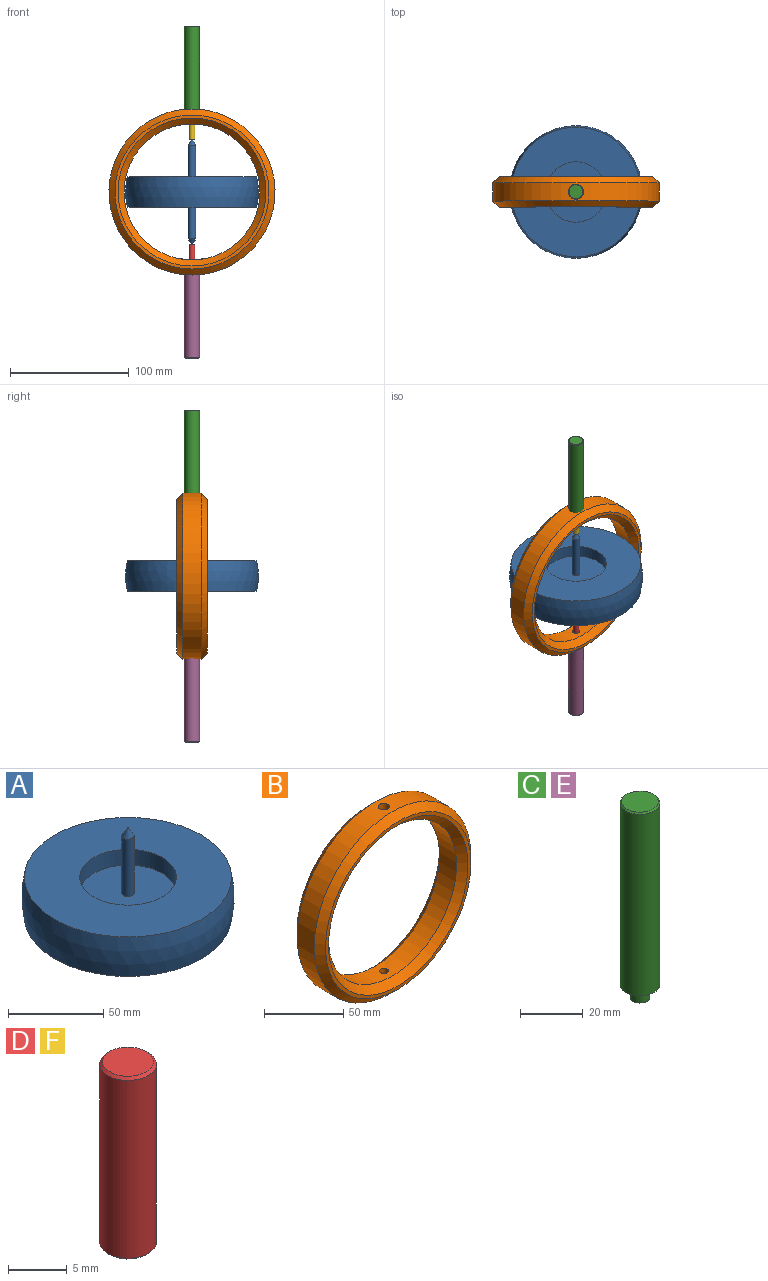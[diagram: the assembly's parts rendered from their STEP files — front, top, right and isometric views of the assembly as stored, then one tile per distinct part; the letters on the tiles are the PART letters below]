
ASSEMBLY  parts=6 mates=4
PART A: 13 faces, bbox 111.8x111.8x88.9 mm
  f0: plane 0.48x0.48mm, normal (0,0,-1), area 0.2mm2, adj f5
  f1: cylinder r=3.17mm len=36.83mm, axis (0,0,-1), area 734.7mm2, adj f2,f5
  f2: plane 50.8x50.8mm, normal (0,0,-1), area 1995.2mm2, adj f1,f3
  f3: cylinder r=25.4mm len=50.8mm, axis (0,0,-1), area 1621.5mm2, adj f2,f4
  f4: plane 108.84x108.84mm, normal (0,0,-1), area 7276.3mm2, adj f3,f6
  f5: cone r=0.24mm half-angle=30deg, axis (0,0,1), area 63mm2, adj f0,f1
  f6: sphere r=55.88mm, area 8918.1mm2, adj f4,f12
  f7: plane 0.48x0.48mm, normal (0,0,1), area 0.2mm2, adj f8
  f8: cone r=3.17mm half-angle=30deg, axis (0,0,-1), area 63mm2, adj f7,f9
  f9: cylinder r=3.17mm len=36.83mm, axis (0,0,-1), area 734.7mm2, adj f8,f10
  f10: plane 50.8x50.8mm, normal (0,0,1), area 1995.2mm2, adj f9,f11
  f11: cylinder r=25.4mm len=50.8mm, axis (0,0,-1), area 1621.5mm2, adj f10,f12
  f12: plane 108.84x108.84mm, normal (0,0,1), area 7276.3mm2, adj f6,f11
PART B: 14 faces, bbox 139.7x25.4x139.7 mm
  f0: cylinder r=69.85mm len=139.7mm, axis (0,1,0), area 6608.9mm2, adj f6,f8,f12,f13
  f1: cylinder r=2.81mm len=5.87mm, axis (0,0,1), area 102.9mm2, adj f3,f9
  f2: cylinder r=2.81mm len=5.87mm, axis (0,0,1), area 102.9mm2, adj f3,f7
  f3: cylinder r=57.15mm len=114.3mm, axis (0,1,0), area 5423.1mm2, adj f1,f2,f10,f11
  f4: plane 129.54x129.54mm, normal (0,-1,0), area 1013.4mm2, adj f11,f12
  f5: plane 129.54x129.54mm, normal (0,1,0), area 1013.4mm2, adj f10,f13
  f6: cylinder r=3.57mm len=7.14mm, axis (0,0,1), area 143.4mm2, adj f0,f7
  f7: cone r=0mm half-angle=59deg, axis (0,0,1), area 17.8mm2, adj f2,f6
  f8: cylinder r=3.57mm len=7.14mm, axis (0,0,-1), area 143.4mm2, adj f0,f9
  f9: cone r=0mm half-angle=59deg, axis (0,0,-1), area 17.8mm2, adj f1,f8
  f10: cone r=62.23mm half-angle=45deg, axis (0,1,0), area 2694.4mm2, adj f3,f5
  f11: cone r=57.15mm half-angle=45deg, axis (0,-1,0), area 2694.4mm2, adj f3,f4
  f12: cone r=64.77mm half-angle=45deg, axis (0,1,0), area 3038.4mm2, adj f0,f4
  f13: cone r=69.85mm half-angle=45deg, axis (0,-1,0), area 3038.4mm2, adj f0,f5
PART C: 6 faces, bbox 12.7x12.7x76.2 mm
  f0: plane 6.35x6.35mm, normal (0,0,-1), area 31.7mm2, adj f1
  f1: cylinder r=3.17mm len=6.35mm, axis (0,0,-1), area 101.3mm2, adj f0,f2
  f2: plane 12.7x12.7mm, normal (0,0,-1), area 95mm2, adj f1,f3
  f3: cylinder r=6.35mm len=70.61mm, axis (0,0,-1), area 2817.3mm2, adj f2,f5
  f4: plane 11.68x11.68mm, normal (0,0,1), area 107.2mm2, adj f5
  f5: cone r=6.35mm half-angle=45deg, axis (0,0,-1), area 27.5mm2, adj f3,f4
PART D: 5 faces, bbox 4.8x4.8x19.1 mm
  f0: plane 4.32x4.32mm, normal (0,0,-1), area 14.6mm2, adj f3
  f1: cylinder r=2.41mm len=18.54mm, axis (0,0,-1), area 281.1mm2, adj f3,f4
  f2: plane 4.32x4.32mm, normal (0,0,1), area 14.6mm2, adj f4
  f3: cone r=2.16mm half-angle=45deg, axis (0,0,1), area 5.2mm2, adj f0,f1
  f4: cone r=2.41mm half-angle=45deg, axis (0,0,-1), area 5.2mm2, adj f1,f2
PART E: same geometry as C
PART F: same geometry as D
PLACE A rot(axis=(0,0,1),158deg) t=(0,-12.7,-0.04)mm
PLACE B at identity fixed
PLACE C rot(axis=(0,0,-1),42.2deg) t=(0,-12.7,63.41)mm
PLACE D rot(axis=(0,0,1),0deg) t=(0,-12.7,-62.98)mm
PLACE E rot(axis=(0.98,-0.19,0),180deg) t=(0,-12.7,-63.41)mm
PLACE F rot(axis=(0,0,1),5.6deg) t=(0,-12.7,44.24)mm
MATE cylindrical B.f1 <-> F.f1  axis (0,0,1) through (0,-12.7,62.95)mm
MATE revolute E.f1 <-> B.f1  axis (0,0,1) through (0,-12.7,-63.41)mm
MATE revolute C.f1 <-> B.f1  axis (0,0,-1) through (0,-12.7,63.41)mm
MATE revolute A.f8 <-> B.f1  axis (0,0,-1) through (0,-12.7,-39.41)mm
